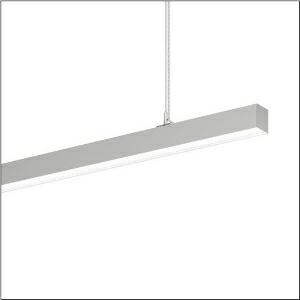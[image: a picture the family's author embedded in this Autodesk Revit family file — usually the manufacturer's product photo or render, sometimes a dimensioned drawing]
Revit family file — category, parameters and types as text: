
# Revit family: silica_r__21_51mx30tbt5s_71cb
name_source: partatom
category: Lighting Fixtures
units: mm (PartAtom-declared; Revit-internal decimal feet)

## family parameters
Cut with Voids When Loaded = No
Host = Face
Light Source = No
Part Type = Normal
Room Calculation Point = No
Round Connector Dimension = Use Diameter
Shared = No

## types (1)
- --- (1 x LED, 5150 lm, 42.2 W, 6500K)
    Apparent Load = 42 VA
    CIE Flux Codes = 47 79 96 58 100
    Color Rendering = 80
    Color Temperature = 6500K
    Default Elevation = 1800 mm
    Description = Silica® 21, office luminaire, primary optical cover: cover, of PMMA, opal, light emission: direct/indirect distribution, primary light characteristic: symmetric, installation type: suspended mounting, LED, rated luminous flux: 5.150lm, luminous efficacy: 116lm/W, light colour: 8tw, colour temperature: 2700..6500K, control gear: ECG DALI, with terminal, 3+2-pole, max. 2.5mm², mains connection: 220..240V, AC, 50/60Hz, rated input power: 44.3W, luminaire housing, of aluminium, metallic grey (RAL 9006), length: 1.504mm, width: 53mm, height: 53mm, protection rating (complete): IP20, insulation class (complete): insulation class I (protective earthing), certification: CE, permissible operating ambient temperature: 0..+35°C, standard: EN 50419, packaging unit: 1 piece
    Height = 53 mm
    Lamp = 1 x LED
    Lamp Light Flux = 5150 lm
    Lamp Power = 42.2 W
    Lamp count = 1
    Length = 1504 mm
    Luminous efficacy = 122 lm/W
    Manufacturer = Siteco
    ModVariant = No
    Model = 51MX30TBT5S
    Mounting Place = Ceiling
    Mounting Type = Pendant
    Number of Poles = 1
    OnlyDefault = Yes
    Power Factor = 1
    Product Name = Silica® 21
    Product group = office luminaire | ceiling pendant
    ProductGroupID = 905
    Protection Class = Protection class I
    Protection Degree = IP 20
    RLX_Detail_Level = 1
    RlxData = <blob elided: 20213 chars, md5=c3575733>
    Socket = socket
    Standby Power = 0 W
    System Light Flux = 5150 lm
    System Power = 42 W
    Type Comments = individual setting
    Type Image = l_1251727.jpg
    URL = http://relux.com
    VarID = @adj_045705
    Voltage = 0 V
    Weight = 0.00 kg
    Width = 53 mm

## geometry (parser evidence)
native form markers: Blend x4, Sweep x11
no freeform markers — native parametric forms only
